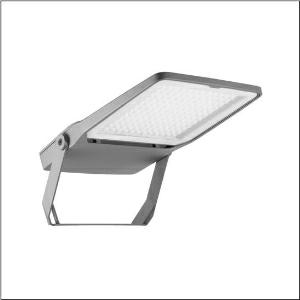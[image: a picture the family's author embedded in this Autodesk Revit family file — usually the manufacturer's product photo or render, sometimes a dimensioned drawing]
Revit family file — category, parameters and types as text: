
# Revit family: floodlight_fl_20_midi___rs17_5xa7682d3b1ac_14e5
name_source: partatom
category: Lighting Fixtures
units: mm (PartAtom-declared; Revit-internal decimal feet)

## family parameters
Cut with Voids When Loaded = No
Host = Face
Light Source = No
Part Type = Normal
Room Calculation Point = No
Round Connector Dimension = Use Diameter
Shared = No

## types (1)
- --- (1 x LED 5000K / CRI = 70 (unbekannt), 19830 lm, 5000K)
    Apparent Load = 142 VA
    CIE Flux Codes = 79 92 99 100 100
    Color Rendering = 70
    Color Temperature = 5000K
    Default Elevation = 1800 mm
    Description = Floodlight FL 20 midi, floodlight, primary light control with lens, of plastic, primary optical cover: protective disc, of toughened safety glass, transparent, light distribution: RS17, light emission: direct distribution, primary light characteristic: rotationally symmetric, installation type: surface-mounted, LED, High Power LED, rated luminous flux: 19.830lm, luminous efficacy: 140lm/W, light colour: 750, colour temperature: 5000K, control gear: ECG Plus, control: flexible luminous flux parameterisation, time-dependent luminous flux control, digital communication interface, power reduction, overheat protection, electronic power reduction, with terminal, 5-pole, max. 2.5mm², mains connection: 220..240V, AC, 50/60Hz, rated input power: 142W, LED unit, of diecast aluminium, powder-coated, Siteco® metallic grey (DB 702S), corrosivity category C5 mid according to DIN EN ISO 12944, incl. 1x M20 cable gland for cable Ø 6.5..12mm, length: 654mm, width: 450mm, height: 76mm, housing frame, of diecast aluminium, powder-coated, Siteco® metallic grey (DB 702S), mounting bracket, of steel, powder-coated, Siteco® metallic grey (DB 702S), DALI, protection rating (complete): IP66, insulation class (complete): insulation class II (safety insulation), certification: CE, ENEC, VDE, protection symbol: D, permissible operating ambient temperature: -40..+40°C, permissible operating ambient temperature for outdoor applications: -40..+50°C, standard: DIN EN 12944, packaging unit: 1 piece

Light Distribution: RS17
    Height = 76 mm
    Lamp = 1 x LED 5000K / CRI >= 70 (unbekannt)
    Lamp Light Flux = 19830 lm
    Lamp count = 1
    Length = 672 mm
    Luminous efficacy = 140 lm/W
    Manufacturer = Siteco
    ModVariant = No
    Model = 5XA7682D3B1AC
    Mounting Place = Wall
    Mounting Type = Surface mounted
    Number of Poles = 1
    OnlyDefault = Yes
    Power Factor = 1
    Product Name = Floodlight FL 20 midi | RS17
    Product group = floodlight | wall mounted
    ProductGroupID = 2001
    Protection Class = Protection class II
    Protection Degree = IP 66
    RLX_Detail_Level = 1
    RLX_Emergency_Light_Flux = 0 lm
    RLX_Emergency_Type = 0
    RLX_Emergency_Type_DB = No
    RlxData = <blob elided: 92257 chars, md5=28030215>
    Socket = socket
    Standby Power = 0 W
    System Light Flux = 19830 lm
    System Power = 142 W
    Type Comments = factory setting: luminous flux: 100 % | dim-lin: 254 | 489 mA
    Type Image = l_1005943.jpg
    URL = http://relux.com
    VarID = @adj_146593
    Voltage = 0 V
    Weight = 0.00 kg
    Width = 450 mm

## geometry (parser evidence)
native form markers: Blend x4, Sweep x12
no freeform markers — native parametric forms only
